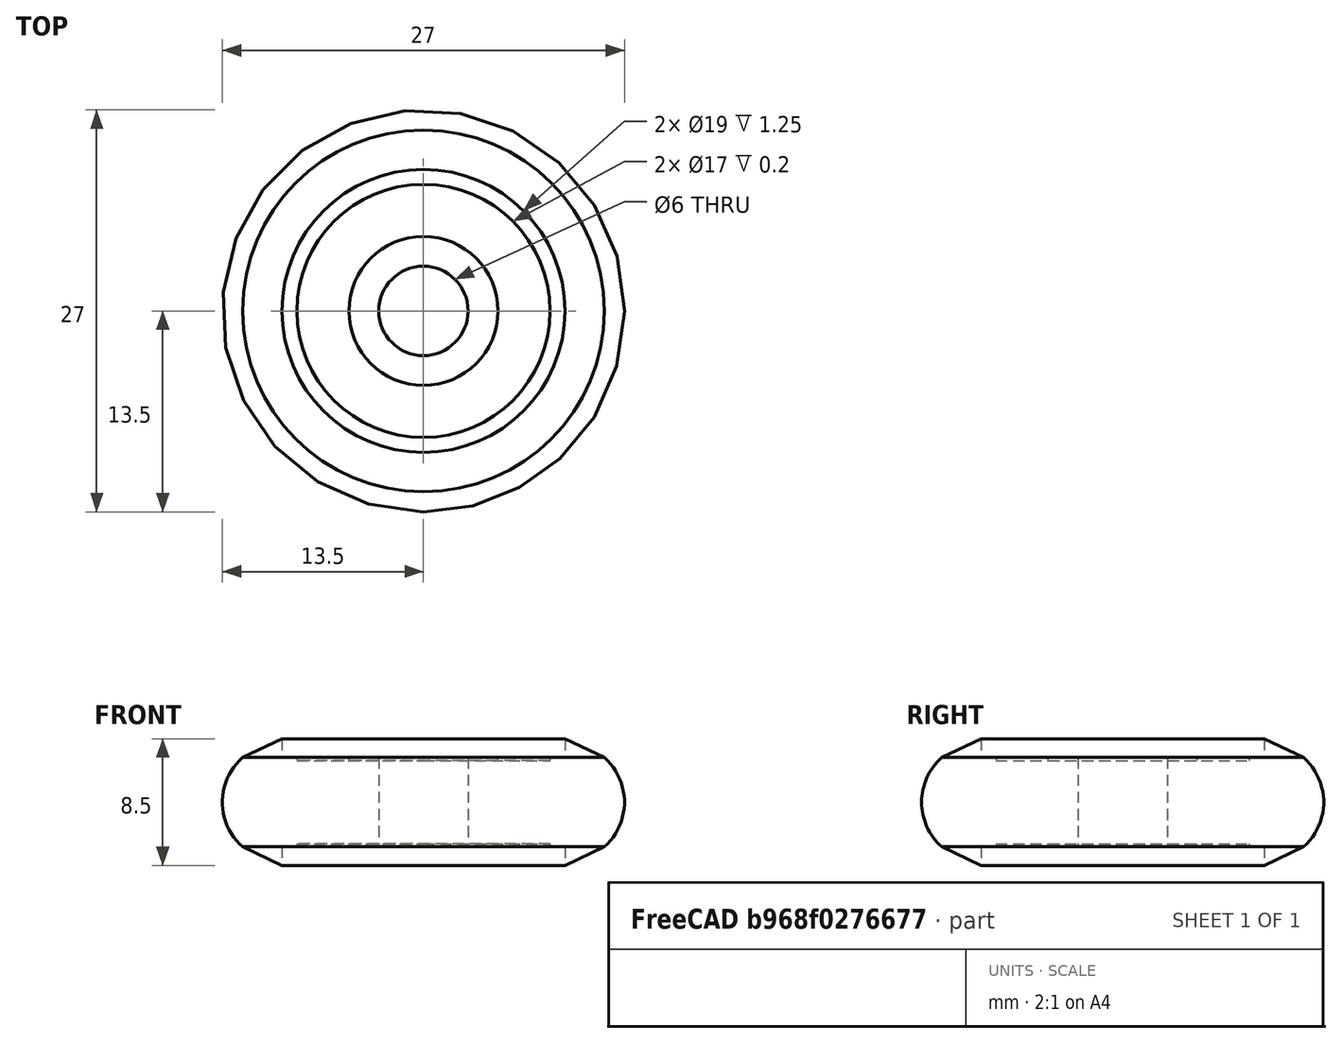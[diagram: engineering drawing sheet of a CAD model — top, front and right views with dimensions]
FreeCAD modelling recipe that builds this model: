
FCSTD DOCUMENT  (FreeCAD 0.19R24276 (Git))
Label: VW0_R6x27x8.5
License: All rights reserved
LicenseURL: http://en.wikipedia.org/wiki/All_rights_reserved
objects: Sketcher::SketchObject×1, PartDesign::Revolution×1, PartDesign::Body×1
note: 4 computed .brp shape members not serialized (recipe doc carries the construction recipe); baked Part::Feature solids carry a one-line shape summary decoded from their .brp

FEATURE [Sketcher::SketchObject] Sketch
  FullyConstrained = true
  MapMode = 5
  Placement = pos=(0,0,0) rot=(0.57735,0.57735,0.57735;2.0944rad)
  Support = -> [YZ_Plane]
  sketch-geometry (19):
    g0: LineSegment StartX=-9.5 StartY=-4.25 StartZ=0 EndX=-12.1458 EndY=-3 EndZ=0
    g1: LineSegment StartX=-12.1458 StartY=3 StartZ=0 EndX=-9.5 EndY=4.25 EndZ=0
    g2: LineSegment StartX=-13.5 StartY=4.25 StartZ=0 EndX=-13.5 EndY=-4.25 EndZ=0
    g3: ArcOfCircle CenterX=-9.5 CenterY=0 CenterZ=0 NormalX=0 NormalY=0 NormalZ=1 AngleXU=0 Radius=4 StartAngle=2.29353 EndAngle=3.98965
    g4: LineSegment StartX=-9.5 StartY=4.25 StartZ=0 EndX=-9.5 EndY=3 EndZ=0
    g5: LineSegment StartX=-5 StartY=2.8 StartZ=0 EndX=-5 EndY=3 EndZ=0
    g6: LineSegment StartX=-5 StartY=3 StartZ=0 EndX=-3 EndY=3 EndZ=0
    g7: LineSegment StartX=-3 StartY=3 StartZ=0 EndX=-3 EndY=-3 EndZ=0
    g8: LineSegment StartX=-3 StartY=-3 StartZ=0 EndX=-5 EndY=-3 EndZ=0
    g9: LineSegment StartX=-5 StartY=-3 StartZ=0 EndX=-5 EndY=-2.8 EndZ=0
    g10: LineSegment StartX=-9.5 StartY=-3 StartZ=0 EndX=-9.5 EndY=-4.25 EndZ=0
    g11: LineSegment StartX=-5 StartY=2.8 StartZ=0 EndX=-5 EndY=-2.8 EndZ=0
    g12: LineSegment StartX=-9.5 StartY=4.25 StartZ=0 EndX=-9.5 EndY=-4.25 EndZ=0
    g13: LineSegment StartX=-9.5 StartY=3 StartZ=0 EndX=-8.5 EndY=3 EndZ=0
    g14: LineSegment StartX=-8.5 StartY=3 StartZ=0 EndX=-8.5 EndY=2.8 EndZ=0
    g15: LineSegment StartX=-8.5 StartY=2.8 StartZ=0 EndX=-5 EndY=2.8 EndZ=0
    g16: LineSegment StartX=-5 StartY=-2.8 StartZ=0 EndX=-8.5 EndY=-2.8 EndZ=0
    g17: LineSegment StartX=-8.5 StartY=-2.8 StartZ=0 EndX=-8.5 EndY=-3 EndZ=0
    g18: LineSegment StartX=-8.5 StartY=-3 StartZ=0 EndX=-9.5 EndY=-3 EndZ=0
  constraints (56):
    c: Vertical(g2)
    c: Coincident(g3,g0)
    c: Coincident(g3,g1)
    c: DistanceX(g2,g-1) = 13.5
    c: Tangent(g2,g3)
    c: Equal(g1,g0)
    c: PointOnObject(g3,g-1)
    c: DistanceY(g0,g1) = 6
    c: DistanceX(g0,g-1) = 9.5
    c: Symmetric(g1,g0,g3)
    c: DistanceY(g0,g1) = 8.5
    c: DistanceY(g2,g2) = 8.5
    c: DistanceY(g-1,g2) = 4.25
    c: Coincident(g1,g4)
    c: Vertical(g4)
    c: Vertical(g5)
    c: Coincident(g5,g6)
    c: Horizontal(g6)
    c: Coincident(g6,g7)
    c: Vertical(g7)
    c: Coincident(g7,g8)
    c: Horizontal(g8)
    c: Coincident(g8,g9)
    c: Vertical(g9)
    c: Coincident(g10,g0)
    c: Vertical(g10)
    c: DistanceX(g7,g-1) = 3
    c: Coincident(g11,g9)
    c: Vertical(g11)
    c: Equal(g5,g9)
    c: DistanceX(g6,g6) = 2
    c: Coincident(g12,g1)
    c: Coincident(g12,g0)
    c: Vertical(g12)
    c: DistanceY(g-1,g6) = 3
    c: DistanceY(g7,g-1) = 3
    c: Coincident(g4,g13)
    c: Horizontal(g13)
    c: Coincident(g13,g14)
    c: Coincident(g14,g15)
    c: Horizontal(g15)
    c: Horizontal(g16)
    c: Coincident(g16,g17)
    c: Vertical(g17)
    c: Coincident(g17,g18)
    c: Coincident(g18,g10)
    c: Horizontal(g18)
    c: Equal(g13,g18)
    c: Equal(g14,g17)
    c: Vertical(g14)
    c: Coincident(g16,g9)
    c: Coincident(g15,g5)
    c: Coincident(g11,g5)
    c: DistanceY(g17,g13) = 6
    c: DistanceX(g13,g13) = 1
    c: DistanceY(g14,g14) = 0.2
FEATURE [PartDesign::Revolution] Revolution
  Angle = 360
  Axis = (-2e-16,3e-16,1)
  Base = (0,0,0)
  Placement = pos=(0,0,0) rot=(0.57735,0.57735,0.57735;2.0944rad)
  Profile = -> Sketch
  ReferenceAxis = -> Sketch [V_Axis]
FEATURE [PartDesign::Body] Body
  Group = -> [Sketch,Revolution]
  Origin = -> Origin
  Tip = -> Revolution
